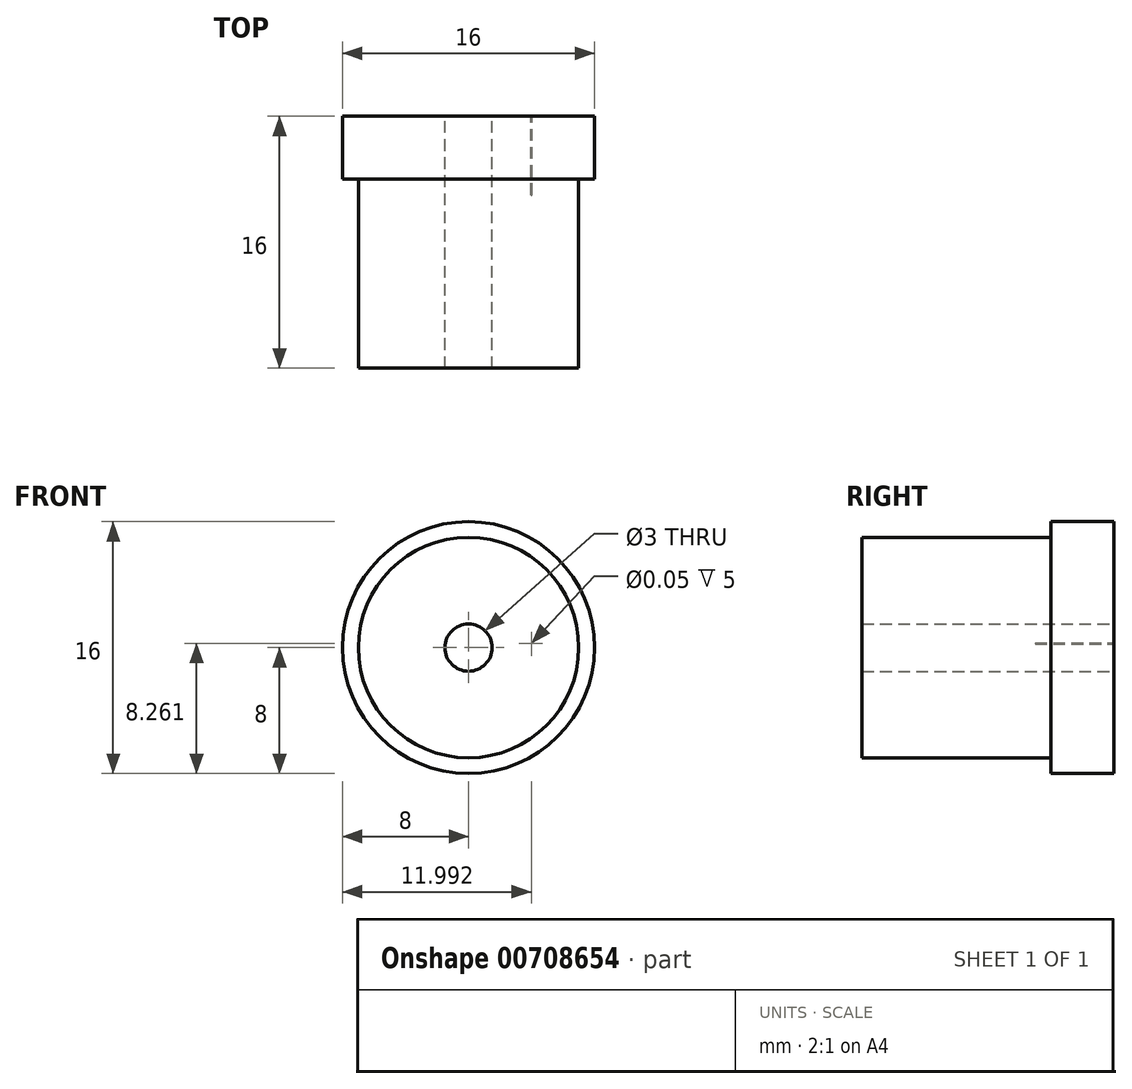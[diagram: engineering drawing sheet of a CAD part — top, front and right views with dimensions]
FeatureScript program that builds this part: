
annotation { "Feature Type Name" : "Feature", "Feature Type Description" : "" }
export const myFeature = defineFeature(function(context is Context, id is Id, definition is map)
    precondition{}
    {
        {
            var Q0;
            Q0=qCreatedBy(makeId("Front.planeOp"),FACE);
            var sketch = newSketch(context, id + "F0", { "sketchPlane" : qUnion([Q0])});
            skCircle(sketch, "E0", {"center": v(0, 0) * mm, "radius": 8 * mm});
            skSolve(sketch);
        }
        {
            var Q0;
            Q0=qSketchRegion(id+"F0",true);
            extrude(context, id + "F1", {"entities" : qUnion([Q0]), "depth" : 4 * mm, "offsetDistance" : 25 * mm});
        }
        {
            var Q0;
            Q0=makeQuery(id+"F1.opExtrude","CAP_FACE",FACE,{"disambiguationData":[OSD([sQuery(id+"F0.wireOp",EDGE,"E0")])],"isStart":false});
            var sketch = newSketch(context, id + "F2", { "sketchPlane" : qUnion([Q0])});
            skCircle(sketch, "E1", {"center": v(0, 0) * mm, "radius": 7 * mm});
            skSolve(sketch);
        }
        {
            var Q0;
            Q0=qSketchRegion(id+"F2",true);
            extrude(context, id + "F3", {"entities" : qUnion([Q0]), "operationType" : NewBodyOperationType.ADD, "depth" : 12 * mm, "offsetDistance" : 25 * mm});
        }
        {
            var Q0;
            Q0=makeQuery(id+"F1.opExtrude","CAP_FACE",FACE,{"disambiguationData":[OSD([sQuery(id+"F0.wireOp",EDGE,"E0")])],"isStart":true});
            var sketch = newSketch(context, id + "F4", { "sketchPlane" : qUnion([Q0])});
            skCircle(sketch, "E2", {"center": v(0, 0) * mm, "radius": 1.5 * mm});
            skSolve(sketch);
        }
        {
            var Q0;
            Q0=qSketchRegion(id+"F4",true);
            extrude(context, id + "F5", {"entities" : qUnion([Q0]), "operationType" : NewBodyOperationType.REMOVE, "endBound" : BoundingType.THROUGH_ALL, "oppositeDirection" : true, "depth" : 25 * mm, "offsetDistance" : 25 * mm});
        }
        {
            var Q0;
            Q0=makeQuery(id+"F1.opExtrude","CAP_FACE",FACE,{"disambiguationData":[OSD([sQuery(id+"F0.wireOp",EDGE,"E0")])],"isStart":true});
            var sketch = newSketch(context, id + "F6", { "sketchPlane" : qUnion([Q0])});
            skCircle(sketch, "E3", {"center": v(-4, 0.26) * mm, "radius": 0.02 * mm});
            skSolve(sketch);
        }
        {
            var Q0;
            Q0=qSketchRegion(id+"F6",true);
            extrude(context, id + "F7", {"entities" : qUnion([Q0]), "operationType" : NewBodyOperationType.REMOVE, "oppositeDirection" : true, "depth" : 5 * mm, "offsetDistance" : 25 * mm});
        }
    });
